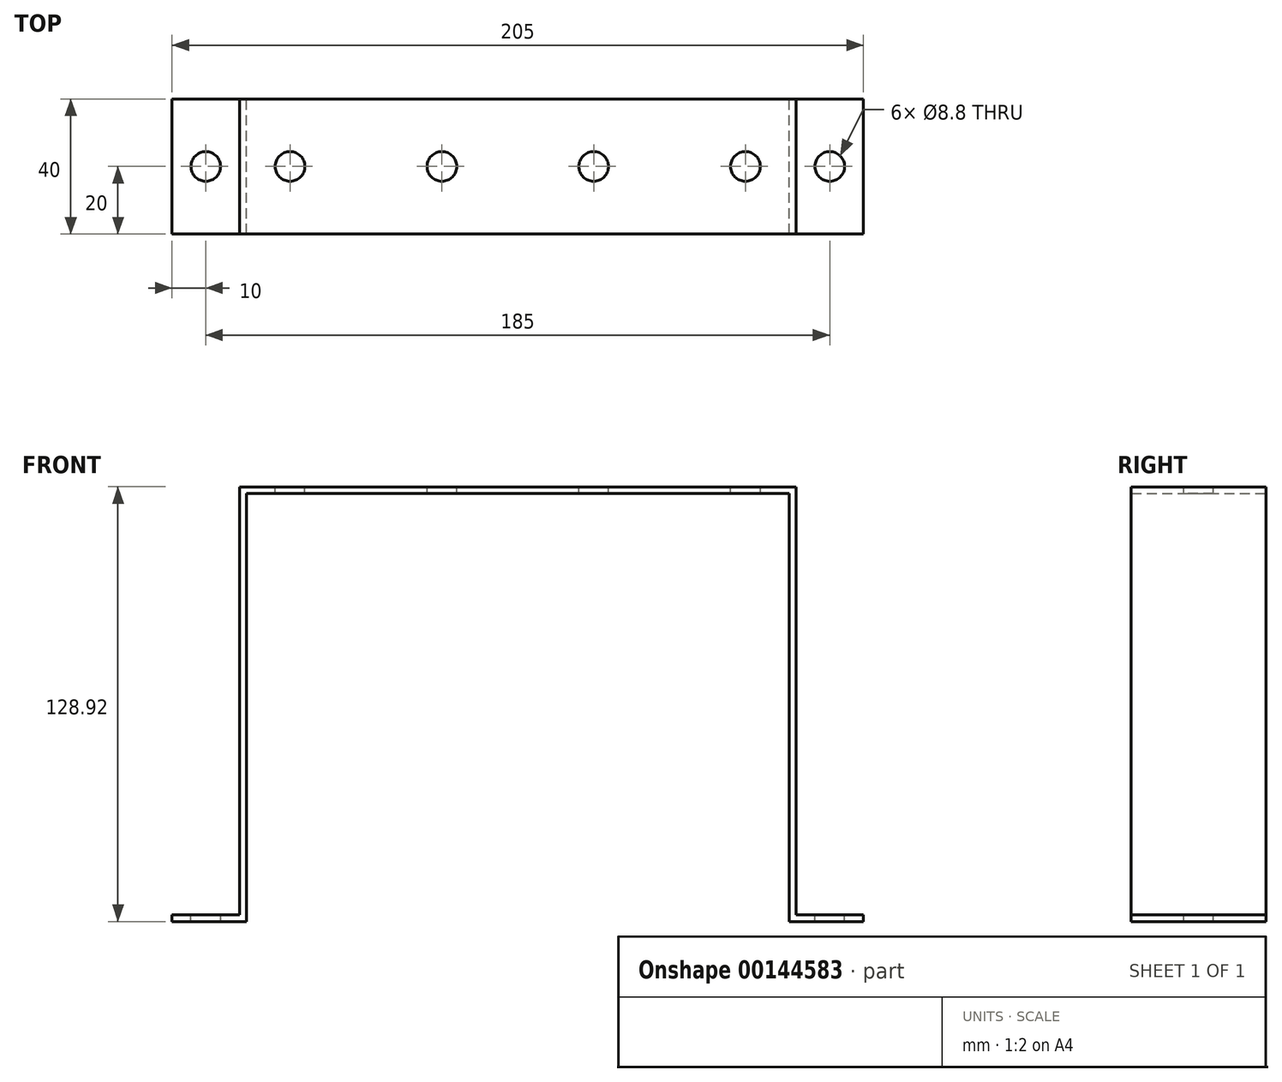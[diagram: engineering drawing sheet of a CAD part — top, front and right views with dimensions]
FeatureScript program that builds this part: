
annotation { "Feature Type Name" : "Feature", "Feature Type Description" : "" }
export const myFeature = defineFeature(function(context is Context, id is Id, definition is map)
    precondition{}
    {
        {
            var Q0;
            Q0=qCreatedBy(makeId("Front.planeOp"),FACE);
            var sketch = newSketch(context, id + "F0", { "sketchPlane" : qUnion([Q0])});
            skLineSegment(sketch, "E0", {"start": v(-90.62, 82.6) * mm, "end": v(74.38, 82.6) * mm});
            skLineSegment(sketch, "E1", {"start": v(-90.62, 82.6) * mm, "end": v(-90.62, -44.32) * mm});
            skLineSegment(sketch, "E2", {"start": v(-90.62, -44.32) * mm, "end": v(-110.62, -44.32) * mm});
            skLineSegment(sketch, "E3.1", {"start": v(-88.62, -46.32) * mm, "end": v(-110.62, -46.32) * mm});
            skLineSegment(sketch, "E3.2", {"start": v(-88.62, 80.6) * mm, "end": v(-88.62, -46.32) * mm});
            skLineSegment(sketch, "E3.3", {"start": v(-88.62, 80.6) * mm, "end": v(72.38, 80.6) * mm});
            skLineSegment(sketch, "E4", {"start": v(-110.62, -46.32) * mm, "end": v(-110.62, -44.32) * mm});
            skLineSegment(sketch, "E5", {"start": v(-8.12, 80.6) * mm, "end": v(-8.12, 61.62) * mm});
            skLineSegment(sketch, "E6.MirrorCS", {"start": v(94.38, -46.32) * mm, "end": v(94.38, -44.32) * mm});
            skLineSegment(sketch, "E7.MirrorCS", {"start": v(72.38, 80.6) * mm, "end": v(72.38, -46.32) * mm});
            skLineSegment(sketch, "E8.MirrorCS", {"start": v(74.38, 82.6) * mm, "end": v(74.38, -44.32) * mm});
            skLineSegment(sketch, "E9.MirrorCS", {"start": v(74.38, -44.32) * mm, "end": v(94.38, -44.32) * mm});
            skLineSegment(sketch, "E10.MirrorCS", {"start": v(72.38, -46.32) * mm, "end": v(94.38, -46.32) * mm});
            skSolve(sketch);
        }
        {
            var Q0;
            Q0=makeQuery(id+"F0.imprint","IMPRINT",FACE,{"disambiguationData":[TD([[makeQuery(id+"F0.imprint","IMPRINT",EDGE,{"derivedFrom":sQuery(id+"F0.wireOp",EDGE,"E0")}),-1.0]])]});
            extrude(context, id + "F1", {"entities" : qUnion([Q0]), "endBound" : BoundingType.SYMMETRIC, "depth" : 40 * mm});
        }
        {
            var Q0;
            Q0=makeQuery(id+"F1.opExtrude","SWEPT_FACE",FACE,{"disambiguationData":[OSD([sQuery(id+"F0.wireOp",EDGE,"E2")])]});
            var sketch = newSketch(context, id + "F2", { "sketchPlane" : qUnion([Q0])});
            skPoint(sketch, "E11", {"position": v(-100.62, 0) * mm});
            skPoint(sketch, "E11.positionSnap0", {"position": v(-100.62, 20) * mm});
            skPoint(sketch, "E11.positionSnap1", {"position": v(-90.62, 0) * mm});
            skSolve(sketch);
        }
        {
            var Q0;
            Q0=makeQuery(id+"F1.opExtrude","SWEPT_FACE",FACE,{"disambiguationData":[OSD([sQuery(id+"F0.wireOp",EDGE,"E0")])]});
            var sketch = newSketch(context, id + "F3", { "sketchPlane" : qUnion([Q0])});
            skLineSegment(sketch, "E12", {"start": v(-8.12, 20) * mm, "end": v(-8.12, 0) * mm});
            skPoint(sketch, "E12.endSnap0", {"position": v(-90.62, 0) * mm});
            skLineSegment(sketch, "E13.1.0.0", {"start": v(14.38, 20) * mm, "end": v(14.38, 0) * mm});
            skLineSegment(sketch, "E13.2.0.0", {"start": v(36.88, 20) * mm, "end": v(36.88, 0) * mm});
            skLineSegment(sketch, "E13.3.0.0", {"start": v(59.38, 20) * mm, "end": v(59.38, 0) * mm});
            skLineSegment(sketch, "E13.direction1", {"start": v(-8.12, 0) * mm, "end": v(14.38, 0) * mm, "construction": true});
            skLineSegment(sketch, "E14.MirrorCS", {"start": v(-30.62, 20) * mm, "end": v(-30.62, 0) * mm});
            skLineSegment(sketch, "E15.MirrorCS", {"start": v(-75.62, 20) * mm, "end": v(-75.62, 0) * mm});
            skSolve(sketch);
        }
        {
            var Q0;
            Q0=makeQuery(id+"F1.opExtrude","SWEPT_FACE",FACE,{"disambiguationData":[OSD([sQuery(id+"F0.wireOp",EDGE,"E9.MirrorCS")])]});
            var sketch = newSketch(context, id + "F4", { "sketchPlane" : qUnion([Q0])});
            skPoint(sketch, "E16", {"position": v(84.38, 0) * mm});
            skPoint(sketch, "E16.positionSnap0", {"position": v(84.38, 20) * mm});
            skPoint(sketch, "E16.positionSnap1", {"position": v(94.38, 0) * mm});
            skSolve(sketch);
        }
        {
            var Q0;
            Q0=sQuery(id+"F3.wireOp",VERTEX,"E15.MirrorCS.end");
            var Q1;
            Q1=sQuery(id+"F3.wireOp",VERTEX,"E14.MirrorCS.end");
            var Q2;
            Q2=sQuery(id+"F3.wireOp",VERTEX,"E13.1.0.0.end");
            var Q3;
            Q3=sQuery(id+"F3.wireOp",VERTEX,"E13.3.0.0.end");
            var Q4;
            Q4=sQuery(id+"F2.wireOp",VERTEX,"E11");
            var Q5;
            Q5=sQuery(id+"F4.wireOp",VERTEX,"E16");
            var Q6;
            Q6=makeQuery(id+"F1.opExtrude","SWEPT_BODY",BODY,{"disambiguationData":[OSD([sQuery(id+"F0.wireOp",EDGE,"E0"),sQuery(id+"F0.wireOp",EDGE,"E1"),sQuery(id+"F0.wireOp",EDGE,"E2"),sQuery(id+"F0.wireOp",EDGE,"2b3b6bcd-0ad3-4797-a0ee-55f789e33f760.MirrorCS"),sQuery(id+"F0.wireOp",EDGE,"2b3b6bcd-0ad3-4797-a0ee-55f789e33f761.MirrorCS"),sQuery(id+"F0.wireOp",EDGE,"E3.0"),sQuery(id+"F0.wireOp",EDGE,"E3.1"),sQuery(id+"F0.wireOp",EDGE,"E3.2"),sQuery(id+"F0.wireOp",EDGE,"E3.3"),sQuery(id+"F0.wireOp",EDGE,"E3.4"),sQuery(id+"F0.wireOp",EDGE,"E4"),sQuery(id+"F0.wireOp",EDGE,"HrgyAWMK-d4EN-vIEF-yjPZ-UVZahJLUWKFk")])]});
            hole(context, id + "F5", {"style" : HoleStyle.SIMPLE, "endStyle" : HoleEndStyle.THROUGH, "standardTappedOrClearance" : lookupTablePath({ "standard" : "ISO", "fit" : "Normal", "size" : "M8", "type" : "Clearance" }), "standardBlindInLast" : lookupTablePath({ "fit" : "Standard", "standard" : "ISO", "size" : "M8", "type" : "Clearance" }), "holeDiameter" : 8.8 * mm, "locations" : qUnion([Q0, Q1, Q2, Q3, Q4, Q5]), "scope" : qUnion([Q6]), "isTappedThrough" : true});
        }
    });
